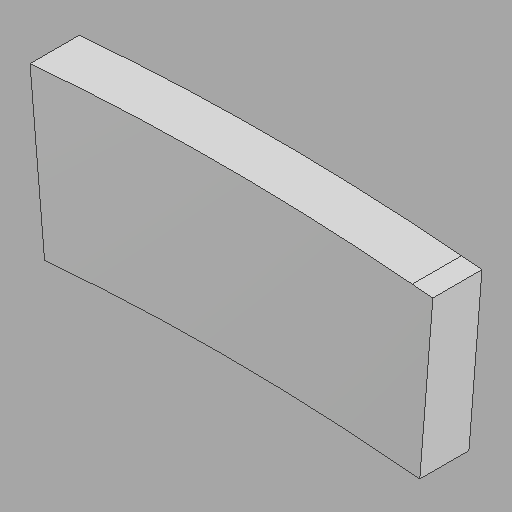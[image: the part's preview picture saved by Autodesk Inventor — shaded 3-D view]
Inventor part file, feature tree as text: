
AUTODESK INVENTOR PART (.ipt)
format: ipt  version: 2022.1 (Build 261234020, 234B)  size: 90,624 bytes
history: imported  units: in
note: dims shown in document units (in); Inventor stores cm internally (conversion verified against a paired STEP export)
features: imported_body x1
ambient origin geometry x8: Origin, YZ Plane, XZ Plane, XY Plane, X Axis, Y Axis, Z Axis, Center Point
bodies: Solid1 (imported_parasolid), Body1 (imported_parasolid)
feature tree (1):
  imported_body  NMx_Import_Brep_tag  [imported B-rep: ~8 faces, bbox_mm=[1249.418368, 511.657745, 152.4]]
